# Revit family: DLB070003
name_source: partatom
category: Appareils sanitaires
revit_build: Autodesk Revit 2015 (Build: 20140606_1530(x64)
units: mm (PartAtom-declared; Revit-internal decimal feet)

## types (1)
- Type 1
    Category = Washbasin
    Commentaires du type = Wall-mounted washbasin with concealed drainage
    Description = French manufacturer Delabie is a leader in the European sanitary ware market for non-domestic places. Water controls, solutions for disabled people, sanitary ware, for schools, leisure centres, offices, hospitals, airports…
    Fabricant = DELABIE
    Features  = Wall-mounted washbasin.
Basin internal diameter: 310mm.
Clean and simple design.
Bacteriostatic 304 stainless steel.
Stainless steel thickness: 1.2mm.
Rounded edges prevent injury.
Vandal-resistant: shrouded basin, concealed trap.
Quick and easy to install from the front thanks to a stainless steel mounting frame.
Supplied with 1¼" waste and trap.
Without overflow.
Supplied with fixing elements.
CE marked. Complies with European standard EN 14688.
Weight: 5.5kg.
    Finish = Polished satin
    Grade = CE
    ManufacturerName = DELABIE
    ManufacturerURL = http://www.delabie.com
    Material = 304 stainless steel
    ModelNumber = 121130
    Modèle = BOB washbasin
    Name = BOB washbasin
    NominalHeight = 285 mm  [stored 0.935039 ft]
    NominalLength = 360 mm  [stored 1.1811 ft]
    NominalWidth = 400 mm  [stored 1.31234 ft]
    ProductInformation = http://www.delabie.com
    Radius = 24 mm
    SerialNumber = 3456330156585
    URL = http://www.delabie.com
    Version = v1
    WarrantyDescription = Any manufacturing defect
    WarrantyDurationUnit = 10 years
    Weight = 5.5kg

note: [stored X ft] marks values corroborated as IEEE doubles in the binary element streams (Revit-internal decimal feet)

## geometry (parser evidence)
native form markers: Blend x14, Sweep x5
no freeform markers — native parametric forms only
